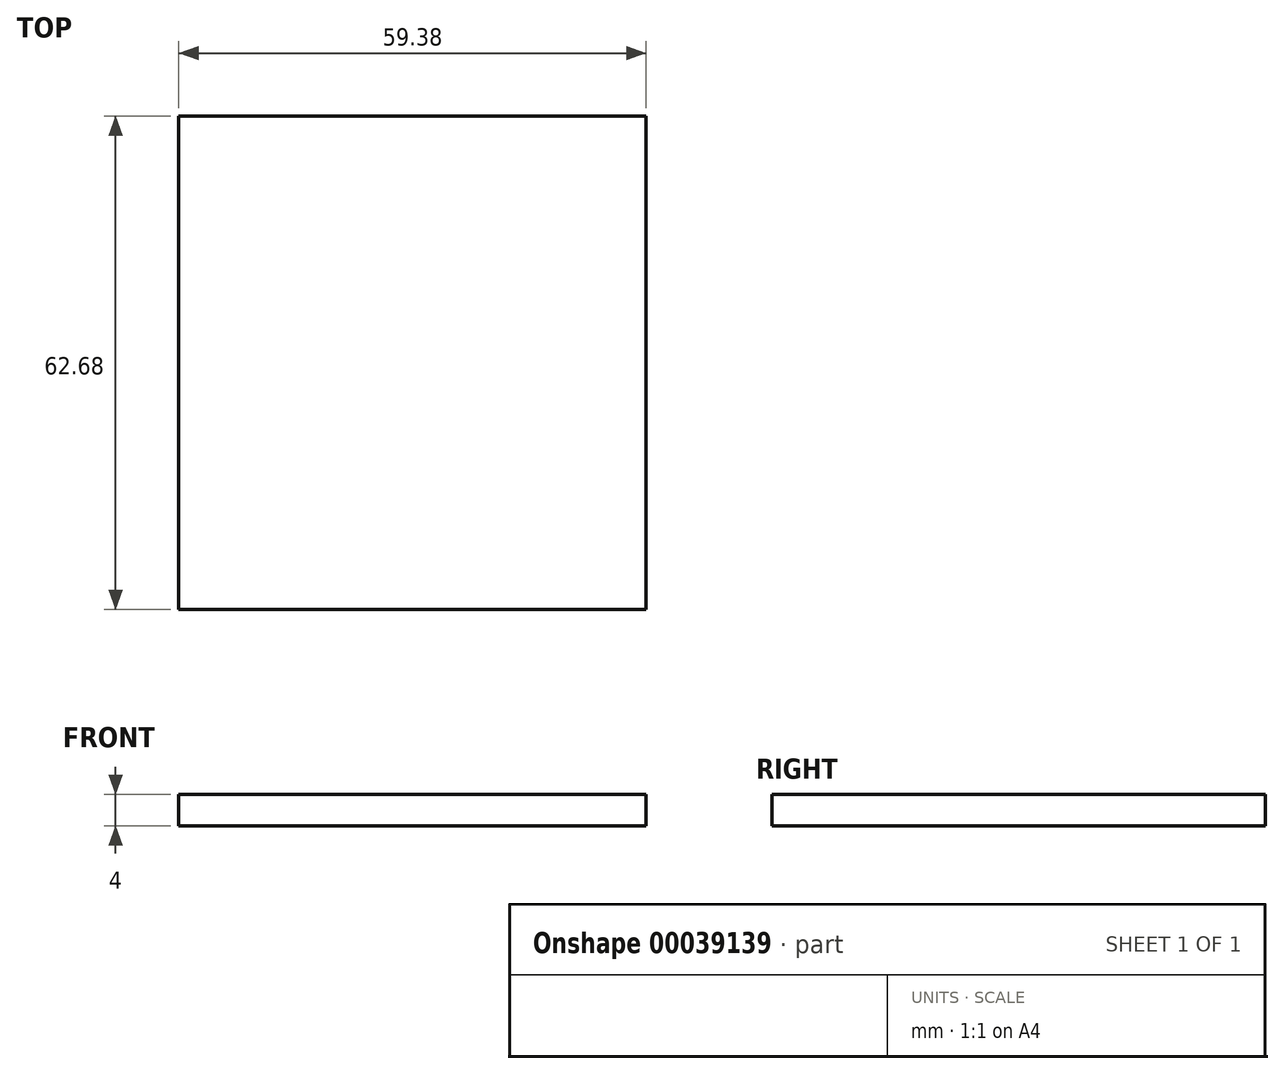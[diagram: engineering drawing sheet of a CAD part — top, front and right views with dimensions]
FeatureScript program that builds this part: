
annotation { "Feature Type Name" : "Feature", "Feature Type Description" : "" }
export const myFeature = defineFeature(function(context is Context, id is Id, definition is map)
    precondition{}
    {
        {
            var Q0;
            Q0=qCreatedBy(makeId("Top.planeOp"),FACE);
            var sketch = newSketch(context, id + "F0", { "sketchPlane" : qUnion([Q0])});
            skLineSegment(sketch, "E0.bottom", {"start": v(-29.69, -31.34) * mm, "end": v(29.69, -31.34) * mm});
            skLineSegment(sketch, "E0.top", {"start": v(-29.69, 31.34) * mm, "end": v(29.69, 31.34) * mm});
            skLineSegment(sketch, "E0.left", {"start": v(-29.69, -31.34) * mm, "end": v(-29.69, 31.34) * mm});
            skLineSegment(sketch, "E0.right", {"start": v(29.69, -31.34) * mm, "end": v(29.69, 31.34) * mm});
            skPoint(sketch, "E0.middle", {"position": v(0, 0) * mm});
            skSolve(sketch);
        }
        {
            var Q0;
            Q0=makeQuery(id+"F0.imprint","IMPRINT",FACE,{"disambiguationData":[TD([[makeQuery(id+"F0.imprint","IMPRINT",EDGE,{"derivedFrom":sQuery(id+"F0.wireOp",EDGE,"E0.bottom")}),1.0]])]});
            extrude(context, id + "F1", {"entities" : qUnion([Q0]), "depth" : 4 * mm, "offsetDistance" : 25 * mm});
        }
    });
